# Revit family: Door-Industrial_Door-Dynaco-M2_Power
name_source: partatom
category: Doors
revit_build: Autodesk Revit 2016 (Build: 20150714_1515(x64)
units: mm (PartAtom-declared; Revit-internal decimal feet)

## family parameters
Always vertical = Yes
Cut with Voids When Loaded = No
Host = Wall
Room Calculation Point = No
Shared = No

## types (2) — shared parameters
Air permeability, EN 12426 = class 1(24 m3/m2/h at 50 Pa)
/m2
/h at 50 Pa
/m2
/h at 50 Pa)
Analytic Construction = <None>
Area of use = Out side
BIMobject category = Industrial Doors
C1 = Yes
C2 = Yes
C3 = Yes
C4 = Yes
C5 = Yes
Closing Speed = 1,2 m/s
Colours = 8 standard colors - white, yellow, green, orange, red, gray, black, blue
Control unit Distance = 600 mm  [stored 1.9685 ft]
Date of publishing = 2015-10-01
Depth = 0.00
Design country = Belgium
Edition number = 1
Five Column Windows = Yes
Five Row Windows = Yes
Four Column Windows = No
Four Row Windows = No
IFC Classification = Door
Lifetime expectations = 1.000.000 cycles
Manufacturer country = Belgium
Manufacturer name = Entrematic
Material main = PVC
Material secondary = Steel
NBS Reference Code = 59-23-38
NBS Reference Description = High Speed Doorsets
Nominal height = 550000
Nominal width = 550000
One Column Windows = No
One Row Windows = No
Opening Speed = up to 2,4 m/s 2
Option 1 = Stainless steel
Options = Different vision options are available, Colour of drum cover, side column cover, motor cover.
Product Guid = f8aa83d8-9e54-480a-8733-59aab485b252
Product SKU = dyn-m2-p
Product data url = https://bimobject.com
Product family = High speed door
Product group = Outside door
QR code = http://bimobject.com
R1 = Yes
R2 = Yes
R3 = Yes
R4 = Yes
R5 = Yes
Reduced Lintel = Yes
Safety = Photocells in side columns,Flexible soft bottom edge including wireless edge activator,Break-away and self-repair function
Flexible soft bottom edge including wireless edge activator
Break-away and self-repair function
Structure = Glavanized steel
Technical description = https://www.dynacodoor.com
Thermal transmittance = 6,02 W/ (m2 K)
K)
Three Column Windows = No
Three Row Windows = No
Two Column Windows = No
Two Row Windows = No
UNSPSC Code = 301715
Uniclass 1.4 Code = L411
Uniclass 1.4 Description = Doors
Uniclass 2.0 Code = PR-59-23-38
Uniclass 2.0 Description = High Speed Doorsets
Unit box = Dynalogic 2 - 380mm x 380mm
Water penetration, EN 12425 = class 2 (50 N/m2)
Wind Load Resistance,EN 12424 = class 3 (700 N/m2),class 4 (1000 N/m2),for doors up to 4000 x 5500 mm
4000 x 5500 mm
) 
)
zero-valued in all types: Weight Net (Kg)

## per-type parameters (varying)
| type | Name of the object | Vision Panel Height |
| Dynaco_M2_Power_400 | Crawford HS8010P high speed door | 400 mm  [stored 1.31234 ft] |
| Dynaco_M2_Power_800 |  | 800 mm  [stored 2.62467 ft] |

note: [stored X ft] marks values corroborated as IEEE doubles in the binary element streams (Revit-internal decimal feet)

## geometry (parser evidence)
native form markers: Blend x2, Sweep x26
no freeform markers — native parametric forms only
